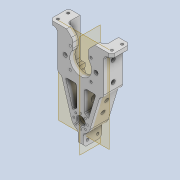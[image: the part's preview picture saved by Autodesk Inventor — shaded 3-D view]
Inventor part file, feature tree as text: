
AUTODESK INVENTOR PART (.ipt)
format: ipt  version: 2020 (Build 240168000, 168)  size: 734,208 bytes
history: native  units: mm
features: extrude x21, sketch x21, projected_geometry x17, fillet x15, thicken_offset x6, chamfer x5, mirror x4, other x4, plane x2, pattern_circular x2, reference x2
ambient origin geometry x8: Origin, YZ Plane, XZ Plane, XY Plane, X Axis, Y Axis, Z Axis, Center Point
bodies: Solid1 (feature_tree)
feature tree (99):
  extrude  "Extrusion1"  Depth=15.0mm
  extrude  "Extrusion2"  Depth=30.0mm
  extrude  "Extrusion3"  Depth=6.0mm
  extrude  "Extrusion4"  Depth=4.0mm TaperAngle=0.0deg
  extrude  "Extrusion5"  Depth=4.0mm TaperAngle=0.0deg
  extrude  "Extrusion6"  Depth=3.0mm
  extrude  "Extrusion7"  Depth=4.0mm
  plane  "Work Plane1"
  extrude  "Extrusion8"  Depth=4.0mm
  chamfer  "Chamfer1"  Distance=10.5mm
  extrude  "Extrusion9"  Depth=30.0mm
  pattern_circular  "Circular Pattern1"  Count=2  [1 undecoded]
  thicken_offset  "Thicken1"
  fillet  "Fillet1"  Radius=80.0mm
  fillet  "Fillet2"  Radius=4.0mm
  extrude  "Extrusion10"  Depth=5.0mm
  pattern_circular  "Circular Pattern2"  [2 undecoded]
  extrude  "Extrusion11"  Depth=1.0mm
  extrude  "Extrusion12"  Depth=10.0mm TaperAngle=0.0deg
  extrude  "Extrusion13"  Depth=1.0mm TaperAngle=360.0deg
  extrude  "Extrusion14"  Depth=10.0mm TaperAngle=0.0deg
  extrude  "Extrusion15"  Depth=1.0mm
  plane  "Work Plane2"
  mirror  "Mirror1"
  extrude  "Extrusion16"  Depth=1.0mm
  extrude  "Extrusion17"  Depth=10.0mm TaperAngle=0.0deg
  mirror  "Mirror2"
  extrude  "Extrusion18"  Depth=1.0mm
  mirror  "Mirror3"
  extrude  "Extrusion19"  Depth=1.0mm
  thicken_offset  "Thicken2"
  extrude  "Extrusion20"  Depth=1.0mm
  fillet  "Fillet3"  Radius=10.0mm
  fillet  "Fillet4"  Radius=6.0mm
  fillet  "Fillet5"  Radius=7.0mm
  fillet  "Fillet6"  Radius=5.0mm
  fillet  "Fillet7"  Radius=10.0mm
  fillet  "Fillet8"  Radius=10.0mm
  chamfer  "Chamfer2"  Distance=10.0mm
  fillet  "Fillet9"  Radius=3.2mm
  thicken_offset  "Thicken3"
  thicken_offset  "Thicken4"
  fillet  "Fillet10"  Radius=3.2mm
  fillet  "Fillet11"  Radius=10.0mm
  fillet  "Fillet12"  Radius=6.0mm
  fillet  "Fillet13"  Radius=14.5mm
  chamfer  "Chamfer3"  Distance=6.0mm
  fillet  "Fillet14"  Radius=14.5mm
  chamfer  "Chamfer4"  Distance=3.0mm
  fillet  "Fillet15"  Radius=4.0mm
  extrude  "Extrusion21"  Depth=1.0mm
  mirror  "Mirror4"
  thicken_offset  "Thicken5"
  thicken_offset  "Thicken6"
  chamfer  "Chamfer5"  Distance=2.0mm
  sketch  "Sketch1"  dims[d0=38.7mm d1=15.0mm]
  reference  "Reference1"
  sketch  "Sketch2"  dims[d2=30.0mm d3=30.0mm]
  sketch  "Sketch3"  dims[d4=19.35mm d5=6.0mm]
  projected_geometry  "Projected Loop1"
  sketch  "Sketch4"  dims[d6=38.7mm d7=4.0mm d8=0.0mm]
  projected_geometry  "Projected Loop2"
  sketch  "Sketch5"  dims[d9=17.0mm d10=4.0mm d11=0.0mm]
  projected_geometry  "Projected Loop3"
  sketch  "Sketch6"  dims[d12=3.0mm d13=3.0mm]
  projected_geometry  "Projected Loop4"
  sketch  "Sketch7"  dims[d14=4.0mm d15=0.0mm d16=4.0mm]
  projected_geometry  "Projected Loop5"
  sketch  "Sketch8"  dims[d17=5.0mm d18=4.0mm]
  sketch  "Sketch9"  dims[d19=5.0mm d20=10.5mm d21=0.0mm]
  projected_geometry  "Projected Loop6"
  sketch  "Sketch10"  dims[d22=14.5mm d23=30.0mm]
  projected_geometry  "Projected Loop7"
  sketch  "Sketch11"  dims[d24=3.0mm d25=0.0mm]
  projected_geometry  "Projected Loop8"
  sketch  "Sketch12"  dims[d26=3.0mm d27=0.0mm]
  reference  "Reference2"
  sketch  "Sketch13"  dims[d28=6.15mm]
  projected_geometry  "Projected Loop9"
  sketch  "Sketch14"  dims[d29=3.0mm d30=0.0mm]
  projected_geometry  "Projected Loop10"
  sketch  "Sketch15"  dims[d31=-2.5mm]
  projected_geometry  "Projected Loop11"
  sketch  "Sketch16"  dims[d32=1.0mm]
  projected_geometry  "Projected Loop12"
  projected_geometry  "Projected Loop13"
  sketch  "Sketch17"  dims[d33=9.0mm d34=0.0mm]
  projected_geometry  "Projected Loop14"
  sketch  "Sketch18"  dims[d35=1.0mm d36=2.0mm d37=45.0deg]
  projected_geometry  "Projected Loop15"
  sketch  "Sketch19"  dims[d38=1.5mm d39=20.0mm d40=0.0mm d41=80.0mm d42=360.0deg d44=4.0mm]
  projected_geometry  "Projected Loop16"
  sketch  "Sketch20"  dims[d45=4.0mm d46=5.0mm]
  sketch  "Sketch21"  dims[d47=3.0mm d48=11.5mm d49=1.8mm d50=10.0mm d51=0.0mm d52=40.0mm d53=360.0deg d55=10.0mm d56=0.0mm d57=20.0mm d58=12.0mm d59=10.0mm d60=0.0mm d61=13.0mm d62=4.0mm d63=12.0mm d64=10.0mm d65=0.0mm d66=6.0mm d67=7.0mm d68=5.0mm d69=10.0mm d70=0.0mm d71=10.0mm d72=10.0mm d73=3.2mm d74=3.2mm d75=10.0mm d76=0.0mm d77=6.0mm d78=14.5mm d79=6.0mm d80=14.5mm d81=3.0mm d82=0.0mm d83=4.0mm d84=4.0mm d85=2.0mm d86=2.0mm d87=3.0mm d88=0.0mm d89=7.0mm d90=15.0mm d91=3.2mm d92=3.2mm d93=3.0mm d94=0.0mm d95=4.0mm d96=2.0mm d97=4.0mm d98=2.0mm d99=4.0mm d100=0.0mm d101=2.0mm d102=2.0mm d103=12.0mm d104=3.2mm d105=12.0mm d106=3.2mm d107=4.0mm d108=0.0mm d109=6.0mm d110=0.5mm d111=1.0mm d112=1.0mm d113=3.0mm d114=2.0mm d115=2.0mm d116=2.0mm d117=45.0deg d118=2.0mm d119=2.0mm d120=2.0mm d121=2.0mm d122=2.0mm d123=1.5mm d124=2.0mm d125=3.0mm d126=4.0mm d127=5.0mm d128=2.0mm d129=45.0deg d130=4.0mm d131=2.0mm d132=2.0mm d133=45.0deg d134=3.0mm d135=5.0mm d136=5.0mm d137=5.0mm d138=5.0mm d139=4.0mm d140=0.0mm d141=0.07mm d142=0.07mm d143=0.07mm d144=0.07mm d145=0.5mm d146=2.0mm d147=45.0deg]
  projected_geometry  "Projected Loop17"
  parser-record x1  (decoder bookkeeping rows leaked as tree rows — omitted from the tree; the rows remain in map.json)
  other  "reducer_unit.iam"
  other  "mot_27_ass:1"
  other  "mot_27_2:1"
note: 3 required parameter values undecoded (feature->parameter linkage not recoverable at this tier; creation-order binding heuristic only, values carry confidence <= 0.55)
note: 1 file-system path scrubbed to <path> (originals preserved in map.json)
